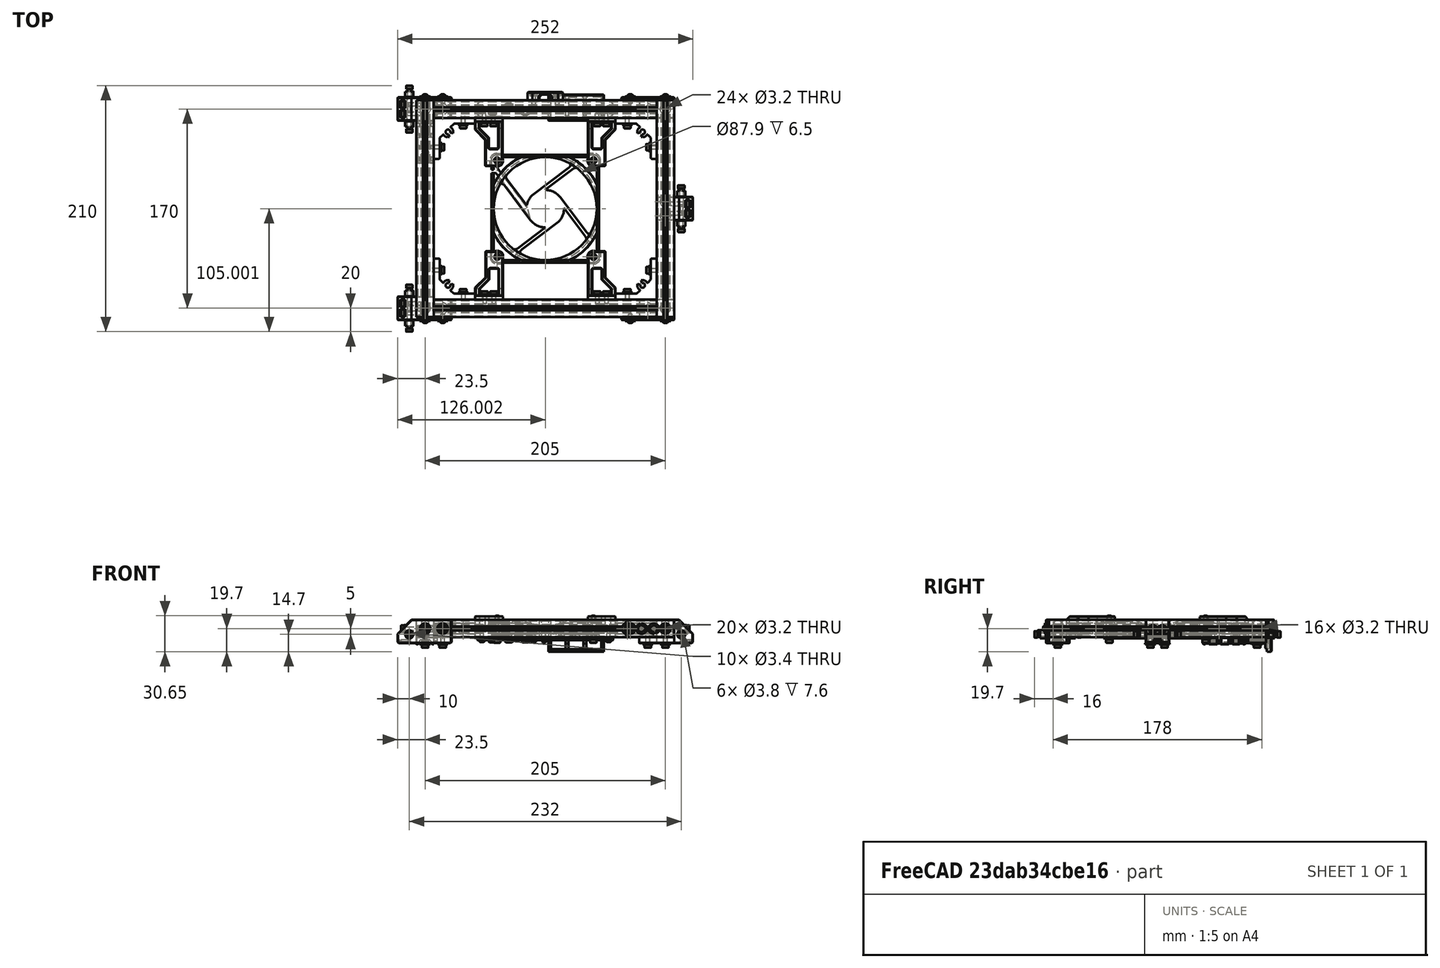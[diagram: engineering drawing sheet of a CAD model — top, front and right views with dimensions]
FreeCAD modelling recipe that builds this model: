
FCSTD DOCUMENT  (FreeCAD 0.19R24291 (Git))
Label: 180-bed-1515-assembly
License: Other
LicenseURL: GPL3
objects: Part::FeaturePython×99, Part::Feature×29, App::Part×1
note: 128 computed .brp shape members not serialized (recipe doc carries the construction recipe); baked Part::Feature solids carry a one-line shape summary decoded from their .brp

FEATURE [Part::Feature] Extrude001001  label="1515-185mm001"
  Placement = pos=(102.5,92.5,-2.1e-14) rot=(1,0,0;1.5708rad)
  shape: bbox 15 x 185 x 15 mm, 71 faces (baked)
FEATURE [Part::Feature] Extrude001002  label="1515-190mm001"
  Placement = pos=(-95,-85,-2.11e-14) rot=(0,1,0;1.5708rad)
  shape: bbox 190 x 15 x 15 mm, 71 faces (baked)
FEATURE [Part::Feature] Extrude001003  label="1515-190mm002"
  Placement = pos=(-95,85,-2.11e-14) rot=(0,1,0;1.5708rad)
  shape: bbox 190 x 15 x 15 mm, 71 faces (baked)
FEATURE [Part::Feature] Extrude001004  label="1515-185mm002"
  Placement = pos=(-102.5,92.5,-2.1e-14) rot=(1,0,0;1.5708rad)
  shape: bbox 15 x 185 x 15 mm, 71 faces (baked)
FEATURE [Part::Feature] Part__Feature  label="_HBLTBS3"
  Placement = pos=(-95,-77.5,-2.11e-14) rot=(0,1,0;1.5708rad)
  shape: bbox 35 x 35 x 9 mm, 26 faces (baked)
FEATURE [Part::Feature] Part__Feature001  label="_HBLTBS004"
  Placement = pos=(-95,77.5,-2.1e-14) rot=(0.57735,0.57735,-0.57735;2.0944rad)
  shape: bbox 35 x 35 x 9 mm, 26 faces (baked)
FEATURE [Part::Feature] Part__Feature002  label="_HBLTBS005"
  Placement = pos=(95,-77.5,2.1e-14) rot=(0.57735,-0.57735,-0.57735;4.18879rad)
  shape: bbox 35 x 35 x 9 mm, 26 faces (baked)
FEATURE [Part::Feature] Part__Feature003  label="_HBLTBS006"
  Placement = pos=(95,77.5,2.1e-14) rot=(0.707107,0,-0.707107;3.14159rad)
  shape: bbox 35 x 35 x 9 mm, 26 faces (baked)
FEATURE [Part::Feature] Fusion001001  label="92mm-slim0fan"
  Placement = pos=(0,2e-15,7.5) rot=(1,0,0;3.14159rad)
  shape: bbox 118.8 x 118.8 x 17.52 mm, 159 faces (baked)
FEATURE [Part::Feature] Part__Mirroring002  label="1515-connector-mounter (Mirror #1)001"
  Placement = pos=(0,75,-7.5) rot=(1,0,0;3.14159rad)
  shape: bbox 116 x 22.25 x 12.2 mm, 276 faces (baked)
FEATURE [Part::Feature] Body001  label="1515-bed-cable-mounter001"
  Placement = pos=(-102.5,57,-7.5) rot=(0,1,0;3.14159rad)
  shape: bbox 15 x 36 x 6 mm, 160 faces (baked)
FEATURE [Part::Feature] Body001001001  label="1515-bed-back-cable-clamp002"
  Placement = pos=(0,92.5,-7.5) rot=(0,0,1;0rad)
  shape: bbox 30 x 8 x 15 mm, 58 faces (baked)
FEATURE [Part::FeaturePython] Washer  label="M3-Washer"  # Fasteners workbench fastener (typed FeaturePython)
  Placement = pos=(-102.5,85,-12.5) rot=(1,0,0;3.14159rad)
  diameter = 1
  invert = true
  matchOuter = true
  offset = 0
  type = 6
FEATURE [Part::FeaturePython] Washer001  label="M3-Washer067"  # Fasteners workbench fastener (typed FeaturePython)
  Placement = pos=(-87.5,85,-12.5) rot=(1,0,0;3.14159rad)
  diameter = 1
  invert = true
  matchOuter = true
  offset = 0
  type = 6
FEATURE [Part::FeaturePython] Washer002  label="M3-Washer072"  # Fasteners workbench fastener (typed FeaturePython)
  Placement = pos=(-102.5,-85,-12.5) rot=(1,0,0;3.14159rad)
  diameter = 1
  invert = false
  matchOuter = true
  offset = 0
  type = 6
FEATURE [Part::FeaturePython] Washer005  label="M3-Washer073"  # Fasteners workbench fastener (typed FeaturePython)
  Placement = pos=(-87.5,-85,-12.5) rot=(1,0,0;3.14159rad)
  diameter = 1
  invert = false
  matchOuter = true
  offset = 0
  type = 6
FEATURE [Part::FeaturePython] Washer006  label="M3-Washer057"  # Fasteners workbench fastener (typed FeaturePython)
  Placement = pos=(87.5,-85,-12.5) rot=(1,0,0;3.14159rad)
  diameter = 1
  invert = false
  matchOuter = true
  offset = 0
  type = 6
FEATURE [Part::FeaturePython] Washer007  label="M3-Washer056"  # Fasteners workbench fastener (typed FeaturePython)
  Placement = pos=(102.5,-85,-12.5) rot=(1,0,0;3.14159rad)
  diameter = 1
  invert = false
  matchOuter = true
  offset = 0
  type = 6
FEATURE [Part::FeaturePython] Washer008  label="M3-Washer062"  # Fasteners workbench fastener (typed FeaturePython)
  Placement = pos=(87.5,85,-12.5) rot=(1,0,0;3.14159rad)
  diameter = 1
  invert = true
  matchOuter = true
  offset = 0
  type = 6
FEATURE [Part::FeaturePython] Washer009  label="M3-Washer061"  # Fasteners workbench fastener (typed FeaturePython)
  Placement = pos=(102.5,85,-12.5) rot=(1,0,0;3.14159rad)
  diameter = 1
  invert = true
  matchOuter = true
  offset = 0
  type = 6
FEATURE [Part::FeaturePython] Washer010  label="M3-Washer079"  # Fasteners workbench fastener (typed FeaturePython)
  Placement = pos=(102.5,-6,-12.5) rot=(1,0,0;3.14159rad)
  diameter = 1
  invert = true
  matchOuter = true
  offset = 0
  type = 6
FEATURE [Part::FeaturePython] Washer011  label="M3-Washer078"  # Fasteners workbench fastener (typed FeaturePython)
  Placement = pos=(102.5,6,-12.5) rot=(1,0,0;3.14159rad)
  diameter = 1
  invert = true
  matchOuter = true
  offset = 0
  type = 6
FEATURE [Part::FeaturePython] Screw  label="M3x10-Screw"  # Fasteners workbench fastener (typed FeaturePython)
  Placement = pos=(-102.5,85,-13.4) rot=(-1,0,0;3.14159rad)
  baseObject = -> Washer [Edge1]
  diameter = 4
  invert = false
  length = 3
  lengthCustom = 10
  matchOuter = true
  offset = 0
  thread = false
  type = 33
FEATURE [Part::FeaturePython] Screw001  label="M3x10-Screw022"  # Fasteners workbench fastener (typed FeaturePython)
  Placement = pos=(-87.5,85,-13.4) rot=(-1,0,0;3.14159rad)
  baseObject = -> Washer001 [Edge1]
  diameter = 4
  invert = false
  length = 3
  lengthCustom = 10
  matchOuter = true
  offset = 0
  thread = false
  type = 33
FEATURE [Part::FeaturePython] Screw002  label="M3x10-Screw023"  # Fasteners workbench fastener (typed FeaturePython)
  Placement = pos=(-102.5,-85,-13.4) rot=(-1,0,0;3.14159rad)
  baseObject = -> Washer002 [Edge1]
  diameter = 4
  invert = false
  length = 3
  lengthCustom = 10
  matchOuter = true
  offset = 0
  thread = false
  type = 33
FEATURE [Part::FeaturePython] Screw003  label="M3x10-Screw024"  # Fasteners workbench fastener (typed FeaturePython)
  Placement = pos=(-87.5,-85,-13.4) rot=(-1,0,0;3.14159rad)
  baseObject = -> Washer005 [Edge1]
  diameter = 4
  invert = false
  length = 3
  lengthCustom = 10
  matchOuter = true
  offset = 0
  thread = false
  type = 33
FEATURE [Part::FeaturePython] Screw004  label="M3x10-Screw018"  # Fasteners workbench fastener (typed FeaturePython)
  Placement = pos=(102.5,-85,-13.4) rot=(1,0,0;3.14159rad)
  baseObject = -> Washer007 [Edge1]
  diameter = 4
  invert = false
  length = 3
  lengthCustom = 10
  matchOuter = true
  offset = 0
  thread = false
  type = 33
FEATURE [Part::FeaturePython] Screw005  label="M3x10-Screw019"  # Fasteners workbench fastener (typed FeaturePython)
  Placement = pos=(87.5,-85,-13.4) rot=(1,0,0;3.14159rad)
  baseObject = -> Washer006 [Edge1]
  diameter = 4
  invert = false
  length = 3
  lengthCustom = 10
  matchOuter = true
  offset = 0
  thread = false
  type = 33
FEATURE [Part::FeaturePython] Screw006  label="M3x10-Screw025"  # Fasteners workbench fastener (typed FeaturePython)
  Placement = pos=(102.5,-6,-13.4) rot=(-1,0,0;3.14159rad)
  baseObject = -> Washer010 [Edge1]
  diameter = 4
  invert = false
  length = 3
  lengthCustom = 10
  matchOuter = true
  offset = 0
  thread = false
  type = 33
FEATURE [Part::FeaturePython] Screw007  label="M3x10-Screw026"  # Fasteners workbench fastener (typed FeaturePython)
  Placement = pos=(102.5,6,-13.4) rot=(-1,0,0;3.14159rad)
  baseObject = -> Washer011 [Edge1]
  diameter = 4
  invert = false
  length = 3
  lengthCustom = 10
  matchOuter = true
  offset = 0
  thread = false
  type = 33
FEATURE [Part::FeaturePython] Screw008  label="M3x10-Screw020"  # Fasteners workbench fastener (typed FeaturePython)
  Placement = pos=(87.5,85,-13.4) rot=(1,0,0;3.14159rad)
  baseObject = -> Washer008 [Edge1]
  diameter = 4
  invert = false
  length = 3
  lengthCustom = 10
  matchOuter = true
  offset = 0
  thread = false
  type = 33
FEATURE [Part::FeaturePython] Screw009  label="M3x10-Screw021"  # Fasteners workbench fastener (typed FeaturePython)
  Placement = pos=(102.5,85,-13.4) rot=(1,0,0;3.14159rad)
  baseObject = -> Washer009 [Edge1]
  diameter = 4
  invert = false
  length = 3
  lengthCustom = 10
  matchOuter = true
  offset = 0
  thread = false
  type = 33
FEATURE [Part::Feature] Body002001  label="1515-92mm-fan-mount001"
  Placement = pos=(60,77.5,10.5) rot=(0,1,0;3.14159rad)
  shape: bbox 23.75 x 42.25 x 18 mm, 72 faces (baked)
FEATURE [Part::Feature] Part__Mirroring003  label="1515-92mm-fan-mount001 (Mirror #1)001"
  Placement = pos=(60,-77.5,10.5) rot=(0,1,0;3.14159rad)
  shape: bbox 23.75 x 42.25 x 18 mm, 72 faces (baked)
FEATURE [Part::Feature] Part__Mirroring001003  label="1515-92mm-fan-mount001 (Mirror #1)002"
  Placement = pos=(-60,77.5,10.5) rot=(1,0,0;3.14159rad)
  shape: bbox 23.75 x 42.25 x 18 mm, 72 faces (baked)
FEATURE [Part::Feature] Body002001003  label="1515-92mm-fan-mount002"
  Placement = pos=(-59.75,-77.5,10.5) rot=(1,0,0;3.14159rad)
  shape: bbox 23.75 x 42.25 x 18 mm, 72 faces (baked)
FEATURE [Part::FeaturePython] Washer012  label="M3-Washer015"  # Fasteners workbench fastener (typed FeaturePython)
  Placement = pos=(-40.9983,-40.9994,-8.5) rot=(1,0,0;3.14159rad)
  baseObject = -> Fusion001001 [Edge373]
  diameter = 4
  invert = false
  matchOuter = true
  offset = 0
  type = 5
FEATURE [Part::FeaturePython] Washer013  label="M3-Washer016"  # Fasteners workbench fastener (typed FeaturePython)
  Placement = pos=(-40.9983,41.0006,-8.5) rot=(1,0,0;3.14159rad)
  baseObject = -> Fusion001001 [Edge369]
  diameter = 4
  invert = false
  matchOuter = true
  offset = 0
  type = 5
FEATURE [Part::FeaturePython] Washer014  label="M3-Washer017"  # Fasteners workbench fastener (typed FeaturePython)
  Placement = pos=(41.0017,41.0006,-8.5) rot=(1,0,0;3.14159rad)
  baseObject = -> Fusion001001 [Edge372]
  diameter = 4
  invert = false
  matchOuter = true
  offset = 0
  type = 5
FEATURE [Part::FeaturePython] Washer015  label="M3-Washer018"  # Fasteners workbench fastener (typed FeaturePython)
  Placement = pos=(41.0017,-40.9994,-8.5) rot=(1,0,0;3.14159rad)
  baseObject = -> Fusion001001 [Edge375]
  diameter = 4
  invert = false
  matchOuter = true
  offset = 0
  type = 5
FEATURE [Part::FeaturePython] Screw010  label="M3x20-Screw"  # Fasteners workbench fastener (typed FeaturePython)
  Placement = pos=(41.0017,-40.9994,-9.05) rot=(1,0,0;3.14159rad)
  baseObject = -> Washer015 [Edge1]
  diameter = 4
  invert = false
  length = 7
  lengthCustom = 20
  matchOuter = true
  offset = 0
  thread = false
  type = 33
FEATURE [Part::FeaturePython] Screw011  label="M3x20-Screw001"  # Fasteners workbench fastener (typed FeaturePython)
  Placement = pos=(-40.9983,-40.9994,-9.05) rot=(1,0,0;3.14159rad)
  baseObject = -> Washer012 [Edge1]
  diameter = 4
  invert = false
  length = 7
  lengthCustom = 20
  matchOuter = true
  offset = 0
  thread = false
  type = 33
FEATURE [Part::FeaturePython] Screw012  label="M3x20-Screw002"  # Fasteners workbench fastener (typed FeaturePython)
  Placement = pos=(-40.9983,41.0006,-9.05) rot=(1,0,0;3.14159rad)
  baseObject = -> Washer013 [Edge1]
  diameter = 4
  invert = false
  length = 7
  lengthCustom = 20
  matchOuter = true
  offset = 0
  thread = false
  type = 33
FEATURE [Part::FeaturePython] Screw013  label="M3x20-Screw003"  # Fasteners workbench fastener (typed FeaturePython)
  Placement = pos=(41.0017,41.0006,-9.05) rot=(1,0,0;3.14159rad)
  baseObject = -> Washer014 [Edge1]
  diameter = 4
  invert = false
  length = 7
  lengthCustom = 20
  matchOuter = true
  offset = 0
  thread = false
  type = 33
FEATURE [Part::Feature] Chamfer004013007011015006009007001005003007001008  label="top-spring-spacer-002"
  Placement = pos=(-116,-70,-5) rot=(1,0,0;1.5708rad)
  shape: bbox 7 x 7 x 7 mm, 14 faces (baked)
FEATURE [Part::Feature] Chamfer002001001  label="top-spring-spacer-001"
  Placement = pos=(-116,-100,-5) rot=(0,0.707107,0.707107;3.14159rad)
  shape: bbox 7 x 7 x 7 mm, 14 faces (baked)
FEATURE [Part::Feature] Chamfer004013007011015006009007001005003007001009  label="top-spring-spacer-003"
  Placement = pos=(-116,100,-5) rot=(1,0,0;1.5708rad)
  shape: bbox 7 x 7 x 7 mm, 14 faces (baked)
FEATURE [Part::Feature] Chamfer004013007011015006009007001005003007001010  label="top-spring-spacer-004"
  Placement = pos=(-116,70,-5) rot=(0,0.707107,0.707107;3.14159rad)
  shape: bbox 7 x 7 x 7 mm, 14 faces (baked)
FEATURE [Part::Feature] Chamfer004013007011015006009007001005003007001012  label="top-spring-spacer-006"
  Placement = pos=(116,15,-5) rot=(1,0,0;1.5708rad)
  shape: bbox 7 x 7 x 7 mm, 14 faces (baked)
FEATURE [Part::Feature] Chamfer004013007011015006009007001005003007001011  label="top-spring-spacer-005"
  Placement = pos=(116,-15,-5) rot=(0,0.707107,0.707107;3.14159rad)
  shape: bbox 7 x 7 x 7 mm, 14 faces (baked)
FEATURE [Part::FeaturePython] Screw014  label="M3x14-Screw"  # Fasteners workbench fastener (typed FeaturePython)
  Placement = pos=(-116,-102,-5) rot=(1,0,0;1.5708rad)
  baseObject = -> Chamfer002001001 [Edge30]
  diameter = 4
  invert = true
  length = 5
  lengthCustom = 14
  matchOuter = true
  offset = 0
  thread = false
  type = 33
FEATURE [Part::FeaturePython] Screw015  label="M3x14-Screw030"  # Fasteners workbench fastener (typed FeaturePython)
  Placement = pos=(-116,-68,-5) rot=(-1,0,0;1.5708rad)
  baseObject = -> Chamfer004013007011015006009007001005003007001008 [Edge30]
  diameter = 4
  invert = true
  length = 5
  lengthCustom = 14
  matchOuter = true
  offset = 0
  thread = false
  type = 33
FEATURE [Part::FeaturePython] Screw016  label="M3x14-Screw024"  # Fasteners workbench fastener (typed FeaturePython)
  Placement = pos=(-116,-102,-5) rot=(1,0,0;1.5708rad)
  baseObject = -> Chamfer002001001 [Edge30]
  diameter = 4
  invert = true
  length = 5
  lengthCustom = 14
  matchOuter = true
  offset = 0
  thread = false
  type = 33
FEATURE [Part::FeaturePython] Screw017  label="M3x14-Screw031"  # Fasteners workbench fastener (typed FeaturePython)
  Placement = pos=(-116,-68,-5) rot=(-1,0,0;1.5708rad)
  baseObject = -> Chamfer004013007011015006009007001005003007001008 [Edge30]
  diameter = 4
  invert = true
  length = 5
  lengthCustom = 14
  matchOuter = true
  offset = 0
  thread = false
  type = 33
FEATURE [Part::FeaturePython] Screw018  label="M3x14-Screw033"  # Fasteners workbench fastener (typed FeaturePython)
  Placement = pos=(-116,102,-5) rot=(-1,0,0;1.5708rad)
  baseObject = -> Chamfer004013007011015006009007001005003007001009 [Edge30]
  diameter = 4
  invert = true
  length = 5
  lengthCustom = 14
  matchOuter = true
  offset = 0
  thread = false
  type = 33
FEATURE [Part::FeaturePython] Screw019  label="M3x14-Screw026"  # Fasteners workbench fastener (typed FeaturePython)
  Placement = pos=(-116,68,-5) rot=(1,0,0;1.5708rad)
  baseObject = -> Chamfer004013007011015006009007001005003007001010 [Edge30]
  diameter = 4
  invert = true
  length = 5
  lengthCustom = 14
  matchOuter = true
  offset = 0
  thread = false
  type = 33
FEATURE [Part::FeaturePython] Screw020  label="M3x14-Screw025"  # Fasteners workbench fastener (typed FeaturePython)
  Placement = pos=(-116,-102,-5) rot=(1,0,0;1.5708rad)
  baseObject = -> Chamfer002001001 [Edge30]
  diameter = 4
  invert = true
  length = 5
  lengthCustom = 14
  matchOuter = true
  offset = 0
  thread = false
  type = 33
FEATURE [Part::FeaturePython] Screw021  label="M3x14-Screw032"  # Fasteners workbench fastener (typed FeaturePython)
  Placement = pos=(-116,-68,-5) rot=(-1,0,0;1.5708rad)
  baseObject = -> Chamfer004013007011015006009007001005003007001008 [Edge30]
  diameter = 4
  invert = true
  length = 5
  lengthCustom = 14
  matchOuter = true
  offset = 0
  thread = false
  type = 33
FEATURE [Part::FeaturePython] Screw022  label="M3x14-Screw034"  # Fasteners workbench fastener (typed FeaturePython)
  Placement = pos=(-116,102,-5) rot=(-1,0,0;1.5708rad)
  baseObject = -> Chamfer004013007011015006009007001005003007001009 [Edge30]
  diameter = 4
  invert = true
  length = 5
  lengthCustom = 14
  matchOuter = true
  offset = 0
  thread = false
  type = 33
FEATURE [Part::FeaturePython] Screw023  label="M3x14-Screw027"  # Fasteners workbench fastener (typed FeaturePython)
  Placement = pos=(-116,68,-5) rot=(1,0,0;1.5708rad)
  baseObject = -> Chamfer004013007011015006009007001005003007001010 [Edge30]
  diameter = 4
  invert = true
  length = 5
  lengthCustom = 14
  matchOuter = true
  offset = 0
  thread = false
  type = 33
FEATURE [Part::FeaturePython] Screw024  label="M3x14-Screw028"  # Fasteners workbench fastener (typed FeaturePython)
  Placement = pos=(116,-17,-5) rot=(1,0,0;1.5708rad)
  baseObject = -> Chamfer004013007011015006009007001005003007001011 [Edge30]
  diameter = 4
  invert = true
  length = 5
  lengthCustom = 14
  matchOuter = true
  offset = 0
  thread = false
  type = 33
FEATURE [Part::FeaturePython] Screw025  label="M3x14-Screw029"  # Fasteners workbench fastener (typed FeaturePython)
  Placement = pos=(116,17,-5) rot=(-1,0,0;1.5708rad)
  baseObject = -> Chamfer004013007011015006009007001005003007001012 [Edge30]
  diameter = 4
  invert = true
  length = 5
  lengthCustom = 14
  matchOuter = true
  offset = 0
  thread = false
  type = 33
FEATURE [Part::FeaturePython] Washer016  label="M3-Washer075"  # Fasteners workbench fastener (typed FeaturePython)
  Placement = pos=(-102.5,-95,0) rot=(1,0,0;1.5708rad)
  diameter = 1
  invert = false
  matchOuter = true
  offset = 0
  type = 6
FEATURE [Part::FeaturePython] Washer017  label="M3-Washer074"  # Fasteners workbench fastener (typed FeaturePython)
  Placement = pos=(-87.5,-95,0) rot=(1,0,0;1.5708rad)
  diameter = 1
  invert = false
  matchOuter = true
  offset = 0
  type = 6
FEATURE [Part::FeaturePython] Washer018  label="M3-Washer065"  # Fasteners workbench fastener (typed FeaturePython)
  Placement = pos=(72.5,-95,2e-15) rot=(1,0,0;1.5708rad)
  diameter = 1
  invert = true
  matchOuter = true
  offset = 0
  type = 6
FEATURE [Part::FeaturePython] Washer019  label="M3-Washer058"  # Fasteners workbench fastener (typed FeaturePython)
  Placement = pos=(102.5,-95,2e-15) rot=(1,0,0;1.5708rad)
  diameter = 1
  invert = true
  matchOuter = true
  offset = 0
  type = 6
FEATURE [Part::FeaturePython] Washer022  label="M3-Washer063"  # Fasteners workbench fastener (typed FeaturePython)
  Placement = pos=(102.5,95,0) rot=(-1,0,0;1.5708rad)
  diameter = 1
  invert = false
  matchOuter = true
  offset = 0
  type = 6
FEATURE [Part::FeaturePython] Washer023  label="M3-Washer066"  # Fasteners workbench fastener (typed FeaturePython)
  Placement = pos=(72.5,95,0) rot=(-1,0,0;1.5708rad)
  diameter = 1
  invert = false
  matchOuter = true
  offset = 0
  type = 6
FEATURE [Part::FeaturePython] Screw026  label="M3x6-Screw"  # Fasteners workbench fastener (typed FeaturePython)
  Placement = pos=(-102.5,-95.9,2e-16) rot=(1,0,0;1.5708rad)
  baseObject = -> Washer016 [Edge1]
  diameter = 1
  invert = false
  length = 0
  lengthCustom = 6
  matchOuter = true
  offset = 0
  thread = false
  type = 39
FEATURE [Part::FeaturePython] Screw027  label="M3x6-Screw037"  # Fasteners workbench fastener (typed FeaturePython)
  Placement = pos=(-87.5,-95.9,2e-16) rot=(1,0,0;1.5708rad)
  baseObject = -> Washer017 [Edge1]
  diameter = 1
  invert = false
  length = 0
  lengthCustom = 6
  matchOuter = true
  offset = 0
  thread = false
  type = 39
FEATURE [Part::FeaturePython] Screw028  label="M3x6-Screw030"  # Fasteners workbench fastener (typed FeaturePython)
  Placement = pos=(72.5,-95.9,2e-15) rot=(1,0,0;1.5708rad)
  baseObject = -> Washer018 [Edge1]
  diameter = 1
  invert = false
  length = 0
  lengthCustom = 6
  matchOuter = true
  offset = 0
  thread = false
  type = 39
FEATURE [Part::FeaturePython] Screw029  label="M3x6-Screw029"  # Fasteners workbench fastener (typed FeaturePython)
  Placement = pos=(102.5,-95.9,2e-15) rot=(1,0,0;1.5708rad)
  baseObject = -> Washer019 [Edge1]
  diameter = 1
  invert = false
  length = 0
  lengthCustom = 6
  matchOuter = true
  offset = 0
  thread = false
  type = 39
FEATURE [Part::FeaturePython] Screw032  label="M3x6-Screw031"  # Fasteners workbench fastener (typed FeaturePython)
  Placement = pos=(102.5,95.9,2e-16) rot=(-1,0,0;1.5708rad)
  baseObject = -> Washer022 [Edge1]
  diameter = 1
  invert = false
  length = 0
  lengthCustom = 6
  matchOuter = true
  offset = 0
  thread = false
  type = 39
FEATURE [Part::FeaturePython] Screw033  label="M3x6-Screw032"  # Fasteners workbench fastener (typed FeaturePython)
  Placement = pos=(72.5,95.9,2e-16) rot=(-1,0,0;1.5708rad)
  baseObject = -> Washer023 [Edge1]
  diameter = 1
  invert = false
  length = 0
  lengthCustom = 6
  matchOuter = true
  offset = 0
  thread = false
  type = 39
FEATURE [Part::FeaturePython] Washer024  label="M3-Washer071"  # Fasteners workbench fastener (typed FeaturePython)
  Placement = pos=(-87.5,95,4e-15) rot=(-1,0,0;1.5708rad)
  diameter = 1
  invert = true
  matchOuter = true
  offset = 0
  type = 6
FEATURE [Part::FeaturePython] Washer025  label="M3-Washer069"  # Fasteners workbench fastener (typed FeaturePython)
  Placement = pos=(-102.5,95,4e-15) rot=(-1,0,0;1.5708rad)
  diameter = 1
  invert = true
  matchOuter = true
  offset = 0
  type = 6
FEATURE [Part::FeaturePython] Screw034  label="M3x6-Screw035"  # Fasteners workbench fastener (typed FeaturePython)
  Placement = pos=(-87.5,95.9,4.2e-15) rot=(-1,0,0;1.5708rad)
  baseObject = -> Washer024 [Edge1]
  diameter = 1
  invert = false
  length = 0
  lengthCustom = 6
  matchOuter = true
  offset = 0
  thread = false
  type = 39
FEATURE [Part::FeaturePython] Screw035  label="M3x6-Screw036"  # Fasteners workbench fastener (typed FeaturePython)
  Placement = pos=(-102.5,95.9,4.2e-15) rot=(-1,0,0;1.5708rad)
  baseObject = -> Washer025 [Edge1]
  diameter = 1
  invert = false
  length = 0
  lengthCustom = 6
  matchOuter = true
  offset = 0
  thread = false
  type = 39
FEATURE [Part::FeaturePython] Washer026  label="M3-Washer068"  # Fasteners workbench fastener (typed FeaturePython)
  Placement = pos=(-119.5,89,0) rot=(0,-1,0;1.5708rad)
  diameter = 4
  invert = false
  matchOuter = true
  offset = 0
  type = 5
FEATURE [Part::FeaturePython] Washer027  label="M3-Washer070"  # Fasteners workbench fastener (typed FeaturePython)
  Placement = pos=(-119.5,81,0) rot=(0,-1,0;1.5708rad)
  diameter = 4
  invert = false
  matchOuter = true
  offset = 0
  type = 5
FEATURE [Part::FeaturePython] Washer028  label="M3-Washer076"  # Fasteners workbench fastener (typed FeaturePython)
  Placement = pos=(-119.5,-81,0) rot=(0,-1,0;1.5708rad)
  diameter = 4
  invert = true
  matchOuter = true
  offset = 0
  type = 5
FEATURE [Part::FeaturePython] Washer029  label="M3-Washer077"  # Fasteners workbench fastener (typed FeaturePython)
  Placement = pos=(-119.5,-89,0) rot=(0,-1,0;1.5708rad)
  diameter = 4
  invert = true
  matchOuter = true
  offset = 0
  type = 5
FEATURE [Part::FeaturePython] Washer030  label="M3-Washer080"  # Fasteners workbench fastener (typed FeaturePython)
  Placement = pos=(119.5,-4,0) rot=(0,1,0;1.5708rad)
  diameter = 4
  invert = true
  matchOuter = true
  offset = 0
  type = 5
FEATURE [Part::FeaturePython] Washer031  label="M3-Washer081"  # Fasteners workbench fastener (typed FeaturePython)
  Placement = pos=(119.5,4,0) rot=(0,1,0;1.5708rad)
  diameter = 4
  invert = true
  matchOuter = true
  offset = 0
  type = 5
FEATURE [Part::FeaturePython] Screw036  label="M3x14-Screw022"  # Fasteners workbench fastener (typed FeaturePython)
  Placement = pos=(120.05,-4,1e-16) rot=(0,1,0;1.5708rad)
  baseObject = -> Washer030 [Edge1]
  diameter = 4
  invert = false
  length = 5
  lengthCustom = 14
  matchOuter = true
  offset = 0
  thread = false
  type = 33
FEATURE [Part::FeaturePython] Screw037  label="M3x14-Screw023"  # Fasteners workbench fastener (typed FeaturePython)
  Placement = pos=(120.05,4,1e-16) rot=(0,1,0;1.5708rad)
  baseObject = -> Washer031 [Edge1]
  diameter = 4
  invert = false
  length = 5
  lengthCustom = 14
  matchOuter = true
  offset = 0
  thread = false
  type = 33
FEATURE [Part::FeaturePython] Screw038  label="M3x14-Screw019"  # Fasteners workbench fastener (typed FeaturePython)
  Placement = pos=(-120.05,89,1e-16) rot=(0,-1,0;1.5708rad)
  baseObject = -> Washer026 [Edge1]
  diameter = 4
  invert = false
  length = 5
  lengthCustom = 14
  matchOuter = true
  offset = 0
  thread = false
  type = 33
FEATURE [Part::FeaturePython] Screw039  label="M3x14-Screw018"  # Fasteners workbench fastener (typed FeaturePython)
  Placement = pos=(-120.05,81,1e-16) rot=(0,-1,0;1.5708rad)
  baseObject = -> Washer027 [Edge1]
  diameter = 4
  invert = false
  length = 5
  lengthCustom = 14
  matchOuter = true
  offset = 0
  thread = false
  type = 33
FEATURE [Part::FeaturePython] Screw040  label="M3x14-Screw021"  # Fasteners workbench fastener (typed FeaturePython)
  Placement = pos=(-120.05,-89,1e-16) rot=(0,-1,0;1.5708rad)
  baseObject = -> Washer029 [Edge1]
  diameter = 4
  invert = false
  length = 5
  lengthCustom = 14
  matchOuter = true
  offset = 0
  thread = false
  type = 33
FEATURE [Part::FeaturePython] Screw041  label="M3x14-Screw020"  # Fasteners workbench fastener (typed FeaturePython)
  Placement = pos=(-120.05,-81,1e-16) rot=(0,-1,0;1.5708rad)
  baseObject = -> Washer028 [Edge1]
  diameter = 4
  invert = false
  length = 5
  lengthCustom = 14
  matchOuter = true
  offset = 0
  thread = false
  type = 33
FEATURE [Part::FeaturePython] Screw042  label="M3x8-Screw"  # Fasteners workbench fastener (typed FeaturePython)
  Placement = pos=(10,96.5,-1e-15) rot=(-1,0,0;1.5708rad)
  baseObject = -> Body001001001 [Edge80]
  diameter = 4
  invert = true
  length = 2
  lengthCustom = 8
  matchOuter = true
  offset = 0
  thread = false
  type = 33
FEATURE [Part::FeaturePython] Screw043  label="M3x8-Screw001"  # Fasteners workbench fastener (typed FeaturePython)
  Placement = pos=(-10,96.5,-1e-15) rot=(-1,0,0;1.5708rad)
  baseObject = -> Body001001001 [Edge118]
  diameter = 4
  invert = true
  length = 2
  lengthCustom = 8
  matchOuter = true
  offset = 0
  thread = false
  type = 33
FEATURE [Part::FeaturePython] Screw044  label="M3x6-Screw013"  # Fasteners workbench fastener (typed FeaturePython)
  Placement = pos=(54,85,-10) rot=(1,0,0;3.14159rad)
  baseObject = -> Part__Mirroring002 [Edge651]
  diameter = 1
  invert = true
  length = 0
  lengthCustom = 6
  matchOuter = true
  offset = 0
  thread = false
  type = 39
FEATURE [Part::FeaturePython] Screw045  label="M3x6-Screw014"  # Fasteners workbench fastener (typed FeaturePython)
  Placement = pos=(-10,85,-10) rot=(1,0,0;3.14159rad)
  baseObject = -> Part__Mirroring002 [Edge178]
  diameter = 1
  invert = true
  length = 0
  lengthCustom = 6
  matchOuter = true
  offset = 0
  thread = false
  type = 39
FEATURE [Part::FeaturePython] Screw046  label="M3x6-Screw015"  # Fasteners workbench fastener (typed FeaturePython)
  Placement = pos=(-54,85,-10) rot=(1,0,0;3.14159rad)
  baseObject = -> Part__Mirroring002 [Edge150]
  diameter = 1
  invert = true
  length = 0
  lengthCustom = 6
  matchOuter = true
  offset = 0
  thread = false
  type = 39
FEATURE [Part::FeaturePython] Washer032  label="M3-Washer044"  # Fasteners workbench fastener (typed FeaturePython)
  Placement = pos=(70,72.5,1.5e-14) rot=(1,0,0;1.5708rad)
  baseObject = -> Part__Feature003 [Edge27]
  diameter = 1
  invert = false
  matchOuter = true
  offset = 0
  type = 6
FEATURE [Part::FeaturePython] Washer033  label="M3-Washer054"  # Fasteners workbench fastener (typed FeaturePython)
  Placement = pos=(90,52.5,2e-14) rot=(0,-1,0;1.5708rad)
  baseObject = -> Part__Feature003 [Edge62]
  diameter = 1
  invert = true
  matchOuter = true
  offset = 0
  type = 6
FEATURE [Part::FeaturePython] Washer034  label="M3-Washer053"  # Fasteners workbench fastener (typed FeaturePython)
  Placement = pos=(-70,72.5,-2.1e-14) rot=(1,0,0;1.5708rad)
  baseObject = -> Part__Feature001 [Edge62]
  diameter = 1
  invert = true
  matchOuter = true
  offset = 0
  type = 6
FEATURE [Part::FeaturePython] Washer035  label="M3-Washer047"  # Fasteners workbench fastener (typed FeaturePython)
  Placement = pos=(-90,52.5,-2.1e-14) rot=(0,1,0;1.5708rad)
  baseObject = -> Part__Feature001 [Edge27]
  diameter = 1
  invert = false
  matchOuter = true
  offset = 0
  type = 6
FEATURE [Part::FeaturePython] Washer036  label="M3-Washer052"  # Fasteners workbench fastener (typed FeaturePython)
  Placement = pos=(-90,-52.5,-2.1e-14) rot=(0,1,0;1.5708rad)
  baseObject = -> Part__Feature [Edge62]
  diameter = 1
  invert = true
  matchOuter = true
  offset = 0
  type = 6
FEATURE [Part::FeaturePython] Washer037  label="M3-Washer049"  # Fasteners workbench fastener (typed FeaturePython)
  Placement = pos=(-70,-72.5,-2.1e-14) rot=(-1,0,0;1.5708rad)
  baseObject = -> Part__Feature [Edge27]
  diameter = 1
  invert = false
  matchOuter = true
  offset = 0
  type = 6
FEATURE [Part::FeaturePython] Washer038  label="M3-Washer055"  # Fasteners workbench fastener (typed FeaturePython)
  Placement = pos=(70,-72.5,2.1e-14) rot=(-1,0,0;1.5708rad)
  baseObject = -> Part__Feature002 [Edge62]
  diameter = 1
  invert = true
  matchOuter = true
  offset = 0
  type = 6
FEATURE [Part::FeaturePython] Washer039  label="M3-Washer051"  # Fasteners workbench fastener (typed FeaturePython)
  Placement = pos=(90,-52.5,2.1e-14) rot=(0,-1,0;1.5708rad)
  baseObject = -> Part__Feature002 [Edge27]
  diameter = 1
  invert = false
  matchOuter = true
  offset = 0
  type = 6
FEATURE [Part::FeaturePython] Screw047  label="M3x10-Screw010"  # Fasteners workbench fastener (typed FeaturePython)
  Placement = pos=(-89.1,-52.5,-2.08e-14) rot=(0,1,0;1.5708rad)
  baseObject = -> Washer036 [Edge1]
  diameter = 4
  invert = false
  length = 3
  lengthCustom = 10
  matchOuter = true
  offset = 0
  thread = false
  type = 33
FEATURE [Part::FeaturePython] Screw048  label="M3x10-Screw011"  # Fasteners workbench fastener (typed FeaturePython)
  Placement = pos=(-70,-71.6,-2.08e-14) rot=(-1,0,0;1.5708rad)
  baseObject = -> Washer037 [Edge1]
  diameter = 4
  invert = false
  length = 3
  lengthCustom = 10
  matchOuter = true
  offset = 0
  thread = false
  type = 33
FEATURE [Part::FeaturePython] Screw049  label="M3x10-Screw012"  # Fasteners workbench fastener (typed FeaturePython)
  Placement = pos=(70,-71.6,2.12e-14) rot=(-1,0,0;1.5708rad)
  baseObject = -> Washer038 [Edge1]
  diameter = 4
  invert = false
  length = 3
  lengthCustom = 10
  matchOuter = true
  offset = 0
  thread = false
  type = 33
FEATURE [Part::FeaturePython] Screw050  label="M3x10-Screw013"  # Fasteners workbench fastener (typed FeaturePython)
  Placement = pos=(89.1,-52.5,2.12e-14) rot=(0,-1,0;1.5708rad)
  baseObject = -> Washer039 [Edge1]
  diameter = 4
  invert = false
  length = 3
  lengthCustom = 10
  matchOuter = true
  offset = 0
  thread = false
  type = 33
FEATURE [Part::FeaturePython] Screw051  label="M3x10-Screw014"  # Fasteners workbench fastener (typed FeaturePython)
  Placement = pos=(89.1,52.5,2e-14) rot=(0,-1,0;1.5708rad)
  baseObject = -> Washer033 [Edge1]
  diameter = 4
  invert = false
  length = 3
  lengthCustom = 10
  matchOuter = true
  offset = 0
  thread = false
  type = 33
FEATURE [Part::FeaturePython] Screw052  label="M3x10-Screw015"  # Fasteners workbench fastener (typed FeaturePython)
  Placement = pos=(70,71.6,1.6e-14) rot=(1,0,0;1.5708rad)
  baseObject = -> Washer032 [Edge1]
  diameter = 4
  invert = false
  length = 3
  lengthCustom = 10
  matchOuter = true
  offset = 0
  thread = false
  type = 33
FEATURE [Part::FeaturePython] Screw053  label="M3x10-Screw016"  # Fasteners workbench fastener (typed FeaturePython)
  Placement = pos=(-70,71.6,-2.08e-14) rot=(1,0,0;1.5708rad)
  baseObject = -> Washer034 [Edge1]
  diameter = 4
  invert = false
  length = 3
  lengthCustom = 10
  matchOuter = true
  offset = 0
  thread = false
  type = 33
FEATURE [Part::FeaturePython] Screw054  label="M3x10-Screw017"  # Fasteners workbench fastener (typed FeaturePython)
  Placement = pos=(-89.1,52.5,-2.08e-14) rot=(0,1,0;1.5708rad)
  baseObject = -> Washer035 [Edge1]
  diameter = 4
  invert = false
  length = 3
  lengthCustom = 10
  matchOuter = true
  offset = 0
  thread = false
  type = 33
FEATURE [Part::FeaturePython] Screw055  label="M3x6-Screw018"  # Fasteners workbench fastener (typed FeaturePython)
  Placement = pos=(-102.5,67,-9.5) rot=(1,0,0;3.14159rad)
  baseObject = -> Body001 [Edge106]
  diameter = 1
  invert = true
  length = 0
  lengthCustom = 6
  matchOuter = true
  offset = 0
  thread = false
  type = 39
FEATURE [Part::FeaturePython] Screw056  label="M3x6-Screw019"  # Fasteners workbench fastener (typed FeaturePython)
  Placement = pos=(-102.5,47.5,-9.5) rot=(1,0,0;3.14159rad)
  baseObject = -> Body001 [Edge350]
  diameter = 1
  invert = true
  length = 0
  lengthCustom = 6
  matchOuter = true
  offset = 0
  thread = false
  type = 39
FEATURE [Part::FeaturePython] Screw057  label="M3x8-Screw002"  # Fasteners workbench fastener (typed FeaturePython)
  Placement = pos=(52,73.5,1.1e-14) rot=(1,0,0;1.5708rad)
  baseObject = -> Body002001 [Edge60]
  diameter = 4
  invert = true
  length = 2
  lengthCustom = 8
  matchOuter = true
  offset = 0
  thread = false
  type = 33
FEATURE [Part::FeaturePython] Screw058  label="M3x8-Screw003"  # Fasteners workbench fastener (typed FeaturePython)
  Placement = pos=(44.25,73.5,1.1e-14) rot=(1,0,0;1.5708rad)
  baseObject = -> Body002001 [Edge61]
  diameter = 4
  invert = true
  length = 2
  lengthCustom = 8
  matchOuter = true
  offset = 0
  thread = false
  type = 33
FEATURE [Part::FeaturePython] Screw059  label="M3x8-Screw004"  # Fasteners workbench fastener (typed FeaturePython)
  Placement = pos=(-44.25,73.5,1.1e-14) rot=(1,0,0;1.5708rad)
  baseObject = -> Part__Mirroring001003 [Edge61]
  diameter = 4
  invert = false
  length = 2
  lengthCustom = 8
  matchOuter = true
  offset = 0
  thread = false
  type = 33
FEATURE [Part::FeaturePython] Screw060  label="M3x8-Screw005"  # Fasteners workbench fastener (typed FeaturePython)
  Placement = pos=(-52,73.5,1.1e-14) rot=(1,0,0;1.5708rad)
  baseObject = -> Part__Mirroring001003 [Edge60]
  diameter = 4
  invert = false
  length = 2
  lengthCustom = 8
  matchOuter = true
  offset = 0
  thread = false
  type = 33
FEATURE [Part::FeaturePython] Screw061  label="M3x8-Screw006"  # Fasteners workbench fastener (typed FeaturePython)
  Placement = pos=(52,-73.5,1.2e-14) rot=(-1,0,0;1.5708rad)
  baseObject = -> Part__Mirroring003 [Edge60]
  diameter = 4
  invert = false
  length = 2
  lengthCustom = 8
  matchOuter = true
  offset = 0
  thread = false
  type = 33
FEATURE [Part::FeaturePython] Screw062  label="M3x8-Screw007"  # Fasteners workbench fastener (typed FeaturePython)
  Placement = pos=(44.25,-73.5,1.2e-14) rot=(-1,0,0;1.5708rad)
  baseObject = -> Part__Mirroring003 [Edge61]
  diameter = 4
  invert = false
  length = 2
  lengthCustom = 8
  matchOuter = true
  offset = 0
  thread = false
  type = 33
FEATURE [Part::FeaturePython] Screw063  label="M3x8-Screw008"  # Fasteners workbench fastener (typed FeaturePython)
  Placement = pos=(-51.75,-73.5,1.1e-14) rot=(-1,0,0;1.5708rad)
  baseObject = -> Body002001003 [Edge60]
  diameter = 4
  invert = true
  length = 2
  lengthCustom = 8
  matchOuter = true
  offset = 0
  thread = false
  type = 33
FEATURE [Part::FeaturePython] Screw064  label="M3x8-Screw009"  # Fasteners workbench fastener (typed FeaturePython)
  Placement = pos=(-44,-73.5,1.1e-14) rot=(-1,0,0;1.5708rad)
  baseObject = -> Body002001003 [Edge61]
  diameter = 4
  invert = true
  length = 2
  lengthCustom = 8
  matchOuter = true
  offset = 0
  thread = false
  type = 33
FEATURE [Part::Feature] Body005001  label="1515-bottom-corner001"
  Placement = pos=(110,-77.5,-12.5) rot=(0,0,1;3.14159rad)
  shape: bbox 30 x 15 x 6 mm, 58 faces (baked)
FEATURE [Part::Feature] Body002001004  label="1515-bottom-corner002"
  Placement = pos=(110,92.5,-12.5) rot=(0,0,1;3.14159rad)
  shape: bbox 30 x 15 x 6 mm, 58 faces (baked)
FEATURE [Part::Feature] Cut028006004005011004003001010002002002001
  Placement = pos=(110,-95,-7.5) rot=(0,0.707107,0.707107;3.14159rad)
  shape: bbox 45 x 3.5 x 15 mm, 345 faces (baked)
FEATURE [Part::Feature] Cut028006004005011004003001010002002002002
  Placement = pos=(110,95,7.5) rot=(0,0.707107,-0.707107;3.14159rad)
  shape: bbox 45 x 3.5 x 15 mm, 345 faces (baked)
FEATURE [Part::Feature] Body005004001  label="1515-corner-arm002"
  Placement = pos=(-110,-85,-12.5) rot=(0,0,1;0rad)
  shape: bbox 46 x 20 x 20 mm, 113 faces (baked)
FEATURE [Part::Feature] Body005003001001  label="1515-corner-arm-rev002"
  Placement = pos=(-110,85,-12.5) rot=(0,0,1;0rad)
  shape: bbox 46 x 20 x 20 mm, 125 faces (baked)
FEATURE [Part::Feature] Body002001001  label="1515-middle-arm002"
  Placement = pos=(110,-1.35e-14,-12.5) rot=(0,0,1;3.14159rad)
  shape: bbox 31 x 20 x 20 mm, 82 faces (baked)
FEATURE [App::Part] Part  label="1515-bed-sammbly"
  Group = -> [Extrude001001,Extrude001002,Extrude001003,Extrude001004,Part__Feature,Part__Feature001,Part__Feature002,Part__Feature003,Fusion001001,Part__Mirroring002,Body001,Body001001001,Screw,Washer001,Screw001,Washer,Screw002,Screw003,Washer005,Washer002,Screw004,Washer007,Screw005,Washer006,Washer009,Screw008,Screw009,Washer008,Washer011,Screw006,Screw007,Washer010,Body002001,Part__Mirroring003,+94 more]
  Origin = -> Origin
